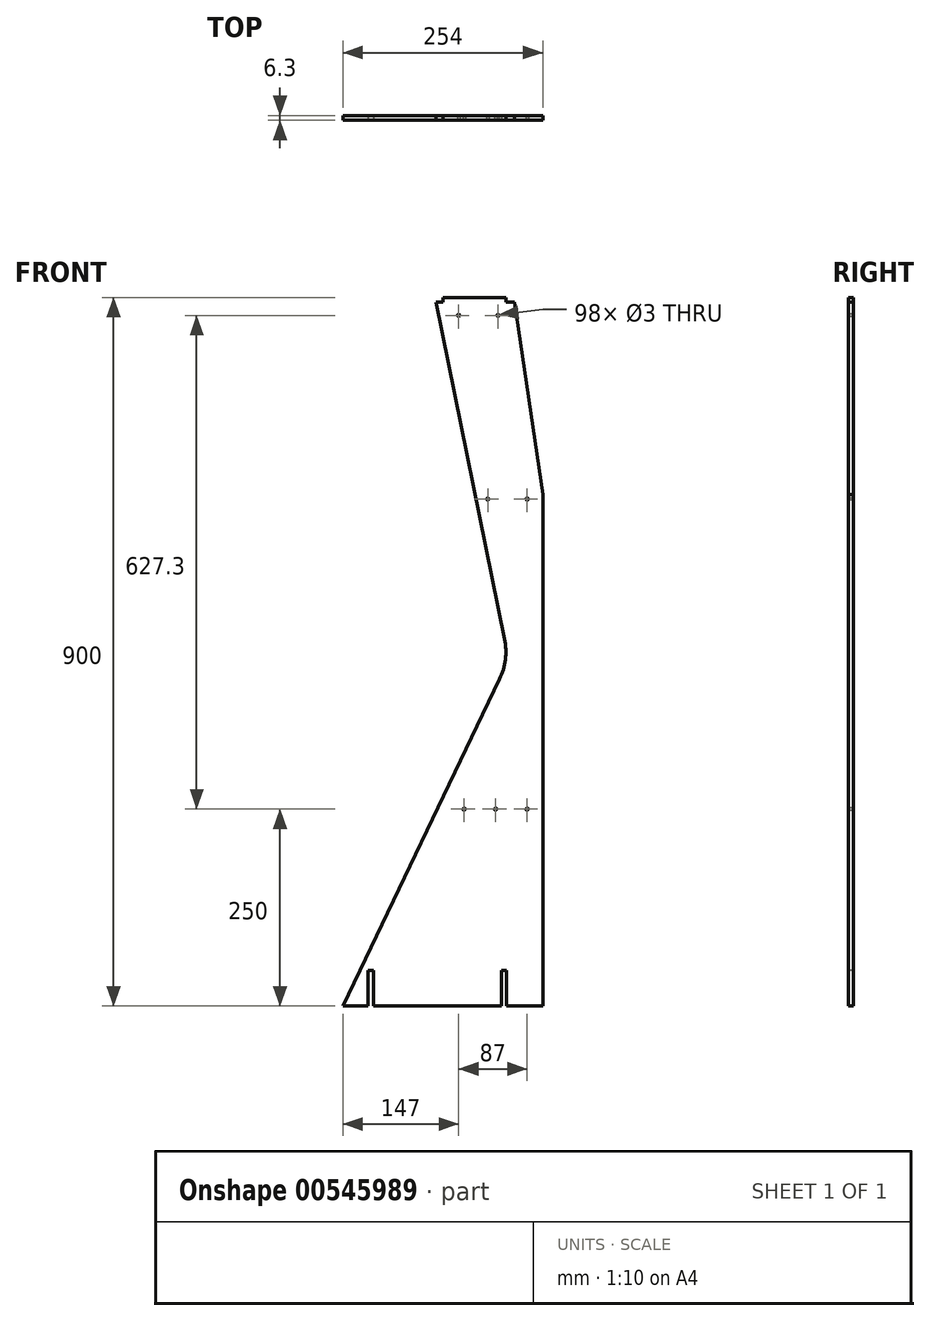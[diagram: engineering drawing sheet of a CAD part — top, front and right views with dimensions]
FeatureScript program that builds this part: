
annotation { "Feature Type Name" : "Feature", "Feature Type Description" : "" }
export const myFeature = defineFeature(function(context is Context, id is Id, definition is map)
    precondition{}
    {
        {
            var Q0;
            Q0=qCreatedBy(makeId("Front.planeOp"),FACE);
            var sketch = newSketch(context, id + "F0", { "sketchPlane" : qUnion([Q0])});
            skLineSegment(sketch, "E0.bottom", {"start": v(-10, 450) * mm, "end": v(90, 450) * mm});
            skLineSegment(sketch, "E0.top", {"start": v(-127, -450) * mm, "end": v(127, -450) * mm});
            skLineSegment(sketch, "E0.right", {"start": v(127, 450) * mm, "end": v(127, -450) * mm, "construction": true});
            skLineSegment(sketch, "E1", {"start": v(-127, 450) * mm, "end": v(127, -450) * mm, "construction": true});
            skArc(sketch, "E2", {"start": v(72.14, -34.58) * mm, "mid": v(79.4, -9.82) * mm, "end": v(78.4, 15.96) * mm});
            skLineSegment(sketch, "E3", {"start": v(-10, 450) * mm, "end": v(78.4, 15.96) * mm});
            skLineSegment(sketch, "E4", {"start": v(-127, -450) * mm, "end": v(72.14, -34.58) * mm});
            skLineSegment(sketch, "E5", {"start": v(90, 450) * mm, "end": v(127, 200) * mm});
            skLineSegment(sketch, "E6", {"start": v(127, 200) * mm, "end": v(127, -450) * mm});
            skSolve(sketch);
        }
        {
            var Q0;
            Q0 = qSketchRegion(id + "F0", true);
            extrude(context, id + "F1", {"entities" : qUnion([Q0]), "endBound" : BoundingType.SYMMETRIC, "depth" : 6.3 * mm, "offsetDistance" : 25 * mm});
        }
        {
            var Q0;
            Q0=makeQuery(id+"F1.opExtrude","CAP_FACE",FACE,{"disambiguationData":[OSD([sQuery(id+"F0.wireOp",EDGE,"E0.bottom"),sQuery(id+"F0.wireOp",EDGE,"E0.top"),sQuery(id+"F0.wireOp",EDGE,"E2"),sQuery(id+"F0.wireOp",EDGE,"E3"),sQuery(id+"F0.wireOp",EDGE,"E4"),sQuery(id+"F0.wireOp",EDGE,"E5"),sQuery(id+"F0.wireOp",EDGE,"E6")])],"isStart":false});
            var sketch = newSketch(context, id + "F2", { "sketchPlane" : qUnion([Q0])});
            skLineSegment(sketch, "E7.bottom", {"start": v(0, 450) * mm, "end": v(-30.61, 450) * mm});
            skLineSegment(sketch, "E7.top", {"start": v(0, 444) * mm, "end": v(-30.61, 444) * mm});
            skLineSegment(sketch, "E7.left", {"start": v(0, 450) * mm, "end": v(0, 444) * mm});
            skLineSegment(sketch, "E7.right", {"start": v(-30.61, 450) * mm, "end": v(-30.61, 444) * mm});
            skLineSegment(sketch, "E8.bottom", {"start": v(80, 450) * mm, "end": v(113.65, 450) * mm});
            skLineSegment(sketch, "E8.top", {"start": v(80, 444) * mm, "end": v(113.65, 444) * mm});
            skLineSegment(sketch, "E8.left", {"start": v(80, 450) * mm, "end": v(80, 444) * mm});
            skLineSegment(sketch, "E8.right", {"start": v(113.65, 450) * mm, "end": v(113.65, 444) * mm});
            skLineSegment(sketch, "E9.bottom", {"start": v(-94.92, -450) * mm, "end": v(-88.32, -450) * mm});
            skLineSegment(sketch, "E9.top", {"start": v(-94.92, -405) * mm, "end": v(-88.32, -405) * mm});
            skLineSegment(sketch, "E9.left", {"start": v(-94.92, -450) * mm, "end": v(-94.92, -405) * mm});
            skLineSegment(sketch, "E9.right", {"start": v(-88.32, -450) * mm, "end": v(-88.32, -405) * mm});
            skLineSegment(sketch, "E10.bottom", {"start": v(81.07, -450) * mm, "end": v(74.47, -450) * mm});
            skLineSegment(sketch, "E10.top", {"start": v(81.07, -405) * mm, "end": v(74.47, -405) * mm});
            skLineSegment(sketch, "E10.left", {"start": v(81.07, -450) * mm, "end": v(81.07, -405) * mm});
            skLineSegment(sketch, "E10.right", {"start": v(74.47, -450) * mm, "end": v(74.47, -405) * mm});
            skSolve(sketch);
        }
        {
            var Q0;
            Q0 = qSketchRegion(id + "F2", true);
            extrude(context, id + "F3", {"entities" : qUnion([Q0]), "operationType" : NewBodyOperationType.REMOVE, "endBound" : BoundingType.THROUGH_ALL, "oppositeDirection" : true, "depth" : 25 * mm, "offsetDistance" : 25 * mm});
        }
        {
            var Q0;
            Q0=makeQuery(id+"F1.opExtrude","CAP_FACE",FACE,{"disambiguationData":[OSD([sQuery(id+"F0.wireOp",EDGE,"E0.bottom"),sQuery(id+"F0.wireOp",EDGE,"E0.top"),sQuery(id+"F0.wireOp",EDGE,"E2"),sQuery(id+"F0.wireOp",EDGE,"E3"),sQuery(id+"F0.wireOp",EDGE,"E4"),sQuery(id+"F0.wireOp",EDGE,"E5"),sQuery(id+"F0.wireOp",EDGE,"E6")])],"isStart":false});
            var sketch = newSketch(context, id + "F4", { "sketchPlane" : qUnion([Q0])});
            skPoint(sketch, "E11", {"position": v(20, 427.3) * mm});
            skPoint(sketch, "E12", {"position": v(70, 427.3) * mm});
            skPoint(sketch, "E13", {"position": v(107, 194) * mm});
            skPoint(sketch, "E14", {"position": v(57, 194) * mm});
            skPoint(sketch, "E15", {"position": v(27, -200) * mm});
            skPoint(sketch, "E16", {"position": v(67, -200) * mm});
            skPoint(sketch, "E17", {"position": v(107, -200) * mm});
            skSolve(sketch);
        }
        {
            var Q0;
            Q0=sQuery(id+"F4.wireOp",VERTEX,"E11");
            var Q1;
            Q1=sQuery(id+"F4.wireOp",VERTEX,"E12");
            var Q2;
            Q2=sQuery(id+"F4.wireOp",VERTEX,"E13");
            var Q3;
            Q3=sQuery(id+"F4.wireOp",VERTEX,"E14");
            var Q4;
            Q4=sQuery(id+"F4.wireOp",VERTEX,"E17");
            var Q5;
            Q5=sQuery(id+"F4.wireOp",VERTEX,"E16");
            var Q6;
            Q6=sQuery(id+"F4.wireOp",VERTEX,"E15");
            var Q7;
            Q7=makeQuery(id+"F1.opExtrude","SWEPT_BODY",BODY,{"disambiguationData":[OSD([sQuery(id+"F0.wireOp",EDGE,"E0.bottom"),sQuery(id+"F0.wireOp",EDGE,"E0.top"),sQuery(id+"F0.wireOp",EDGE,"E2"),sQuery(id+"F0.wireOp",EDGE,"E3"),sQuery(id+"F0.wireOp",EDGE,"E4"),sQuery(id+"F0.wireOp",EDGE,"E5"),sQuery(id+"F0.wireOp",EDGE,"E6")])]});
            hole(context, id + "F5", {"style" : HoleStyle.SIMPLE, "endStyle" : HoleEndStyle.THROUGH, "holeDiameter" : 3 * mm, "isTappedThrough" : true, "tappedDepth" : 12 * mm, "tapClearance" : 3, "locations" : qUnion([Q0, Q1, Q2, Q3, Q4, Q5, Q6]), "scope" : qUnion([Q7])});
        }
    });
